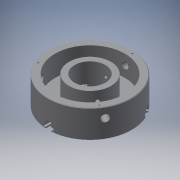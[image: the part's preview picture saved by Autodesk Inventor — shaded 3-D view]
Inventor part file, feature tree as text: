
AUTODESK INVENTOR PART (.ipt)
format: ipt  version: 2016 (Build 200138000, 138)  size: 268,800 bytes
history: native  units: in
note: dims shown in document units (in); Inventor stores cm internally (conversion verified against a paired STEP export)
features: sketch x5, extrude x4, plane x2, revolve x1, other x1, pattern_circular x1, chamfer x1, projected_geometry x1, reference x1
ambient origin geometry x8: Origin, YZ Plane, XZ Plane, XY Plane, X Axis, Y Axis, Z Axis, Center Point
bodies: Solid1 (feature_tree)
feature tree (17):
  revolve  "Revolution3"  [1 undecoded]
  extrude  "Extrusion8"  Depth=0.1969in
  plane  "Work Plane1"
  extrude  "Extrusion12"  Depth=0.5906in
  extrude  "Extrusion13"  Depth=0.0787in
  plane  "Work Plane2"
  other  "Work Axis2"
  extrude  "Extrusion14"  Depth=1.1811in
  pattern_circular  "Circular Pattern1"  [2 undecoded]
  chamfer  "Chamfer1"  Distance=0.0394in
  sketch  "Sketch10"  dims[d51=0.5906in d52=0.1575in]
  sketch  "Sketch11"  dims[d53=0.9843in d54=0.1969in]
  projected_geometry  "Projected Loop1"
  sketch  "Sketch15"  dims[d55=0.1969in d56=0.5906in]
  reference  "Reference2"
  sketch  "Sketch16"  dims[d58=90.0deg d60=0.0787in]
  sketch  "Sketch17"  dims[d61=0.0787in d62=0.1378in d63=0.0787in d64=0.0394in d65=0.3937in d66=0.0in d67=0.0in d68=0.0787in d69=0.0in d72=-1.378in d78=0.3937in d79=0.0in d80=0.3937in d81=0.0in d82=-1.1811in d83=0.1969in d84=0.3937in d85=0.0in d86=0.0394in d87=1.1811in d88=360.0deg d90=0.0157in d91=0.0787in d92=45.0deg]
note: 3 required parameter values undecoded (feature->parameter linkage not recoverable at this tier; creation-order binding heuristic only, values carry confidence <= 0.55)